# Revit family: DF_ЗажимСоединительный_Пруток-Пруток_8-10_EZETEK
name_source: partatom
category: Соединительные детали воздуховодов
revit_build: Autodesk Revit 2017 (Build: 20170118_1100(x64)
units: mm (PartAtom-declared; Revit-internal decimal feet)

## family parameters
Всегда вертикально = Да
На основе рабочей плоскости = Нет
Общий = Нет
При загрузке вырезать с полостями = Нет
Размер круглого соединителя = Использовать радиус
Тип детали = Соединение

## types (3) — shared parameters
ADSK_Версия Revit = 2017
ADSK_Единица измерения = Неспецифицируемое
ADSK_Завод-изготовитель = Неспецифицируемое
ADSK_Код изделия = Неспецифицируемое
ADSK_Марка = Неспецифицируемое
ADSK_Масса_Текст = Неспецифицируемое
ADSK_Наименование = Неспецифицируемое
ADSK_Обозначение = Неспецифицируемое
URL = https://ezetek.ru
Группа модели = Зажимы
Изготовитель = Ezetek
Описание = Зажимы позволяют соединять пруток молниезащитной сетки и токоотводов диаметром 8-10 мм в перпендикулярном направлении, в параллельном направлении, а также под произвольным углом.
zero-valued in all types: ADSK_Количество, ADSK_Масса

## per-type parameters (varying)
| type | ADSK_Материал | Тип |
| ЗажимСоединительный_Пруток-Пруток_Латунь_91072 | BIMLIB_Латунь_EZETEK | FA_ЗажимСоединительный_Пруток-Пруток_8-10_EZETEK : ЗажимСоединительный_Пруток-Пруток_Латунь_91072 |
| ЗажимСоединительный_Пруток-Пруток_Медь_91070 | BIMLIB_Медь_EZETEK | FA_ЗажимСоединительный_Пруток-Пруток_8-10_EZETEK : ЗажимСоединительный_Пруток-Пруток_Медь_91070 |
| ЗажимСоединительный_Пруток-Пруток_Оцинк_91071 | BIMLIB_Сталь_Оцинкованная_EZETEK | FA_ЗажимСоединительный_Пруток-Пруток_8-10_EZETEK : ЗажимСоединительный_Пруток-Пруток_Оцинк_91071 |
